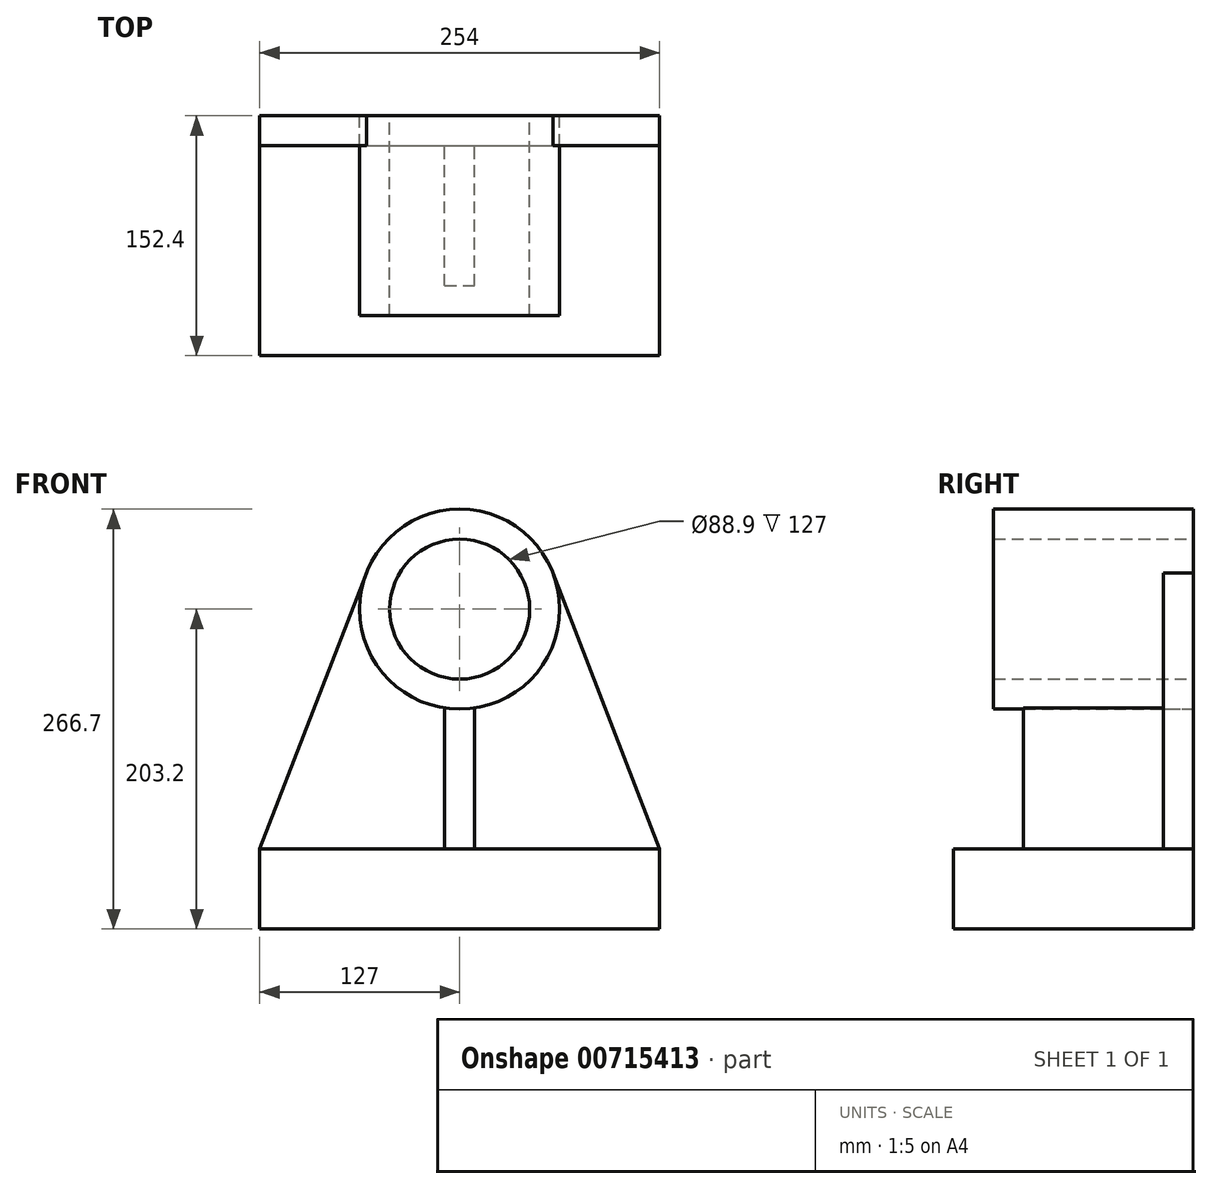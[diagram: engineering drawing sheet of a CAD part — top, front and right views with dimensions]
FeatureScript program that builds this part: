
annotation { "Feature Type Name" : "Feature", "Feature Type Description" : "" }
export const myFeature = defineFeature(function(context is Context, id is Id, definition is map)
    precondition{}
    {
        {
            var Q0;
            Q0=qCreatedBy(makeId("Front.planeOp"),FACE);
            var sketch = newSketch(context, id + "F0", { "sketchPlane" : qUnion([Q0])});
            skCircle(sketch, "E0", {"center": v(0, 0) * mm, "radius": 63.5 * mm});
            skCircle(sketch, "E1", {"center": v(0, 0) * mm, "radius": 44.45 * mm});
            skSolve(sketch);
        }
        {
            var Q0;
            Q0=makeQuery(id+"F0.imprint","IMPRINT",FACE,{"disambiguationData":[TD([[makeQuery(id+"F0.imprint","IMPRINT",EDGE,{"derivedFrom":sQuery(id+"F0.wireOp",EDGE,"E0")}),1.0]])]});
            extrude(context, id + "F1", {"entities" : qUnion([Q0]), "depth" : 127 * mm, "offsetDistance" : 25.4 * mm});
        }
        {
            var Q0;
            Q0=qCreatedBy(makeId("Front.planeOp"),FACE);
            var sketch = newSketch(context, id + "F2", { "sketchPlane" : qUnion([Q0])});
            skLineSegment(sketch, "E2", {"start": v(-59.23, 22.9) * mm, "end": v(-127, -152.4) * mm});
            skLineSegment(sketch, "E3", {"start": v(-127, -152.4) * mm, "end": v(127, -152.4) * mm});
            skLineSegment(sketch, "E4", {"start": v(127, -152.4) * mm, "end": v(59.23, 22.9) * mm});
            skArc(sketch, "E5", {"start": v(-59.23, 22.9) * mm, "mid": v(0, -63.5) * mm, "end": v(59.23, 22.9) * mm});
            skSolve(sketch);
        }
        {
            var Q0;
            Q0 = qSketchRegion(id + "F2", true);
            extrude(context, id + "F3", {"entities" : qUnion([Q0]), "depth" : 19.05 * mm, "offsetDistance" : 25.4 * mm});
        }
        {
            var Q0;
            Q0=qCreatedBy(makeId("Front.planeOp"),FACE);
            var sketch = newSketch(context, id + "F4", { "sketchPlane" : qUnion([Q0])});
            skLineSegment(sketch, "E6.bottom", {"start": v(-127, -152.4) * mm, "end": v(127, -152.4) * mm});
            skLineSegment(sketch, "E6.top", {"start": v(-127, -203.2) * mm, "end": v(127, -203.2) * mm});
            skLineSegment(sketch, "E6.left", {"start": v(-127, -152.4) * mm, "end": v(-127, -203.2) * mm});
            skLineSegment(sketch, "E6.right", {"start": v(127, -152.4) * mm, "end": v(127, -203.2) * mm});
            skSolve(sketch);
        }
        {
            var Q0;
            Q0=makeQuery(id+"F4.imprint","IMPRINT",FACE,{"disambiguationData":[TD([[makeQuery(id+"F4.imprint","IMPRINT",EDGE,{"derivedFrom":sQuery(id+"F4.wireOp",EDGE,"E6.bottom")}),-1.0]])]});
            extrude(context, id + "F5", {"entities" : qUnion([Q0]), "operationType" : NewBodyOperationType.ADD, "depth" : 152.4 * mm, "offsetDistance" : 25.4 * mm});
        }
        {
            var Q0;
            Q0=makeQuery(id+"F3.opExtrude","CAP_FACE",FACE,{"disambiguationData":[OSD([sQuery(id+"F2.wireOp",EDGE,"E2"),sQuery(id+"F2.wireOp",EDGE,"E3"),sQuery(id+"F2.wireOp",EDGE,"E4"),sQuery(id+"F2.wireOp",EDGE,"E5")])],"isStart":false});
            var sketch = newSketch(context, id + "F6", { "sketchPlane" : qUnion([Q0])});
            skLineSegment(sketch, "E7", {"start": v(-9.53, -152.4) * mm, "end": v(9.53, -152.4) * mm});
            skLineSegment(sketch, "E8", {"start": v(9.53, -152.4) * mm, "end": v(9.53, -62.78) * mm});
            skLineSegment(sketch, "E9", {"start": v(-9.53, -152.4) * mm, "end": v(-9.53, -62.78) * mm});
            skArc(sketch, "E10", {"start": v(-9.53, -62.78) * mm, "mid": v(0, -63.5) * mm, "end": v(9.53, -62.78) * mm});
            skSolve(sketch);
        }
        {
            var Q0;
            Q0=makeQuery(id+"F6.imprint","IMPRINT",FACE,{"disambiguationData":[TD([[makeQuery(id+"F6.imprint","IMPRINT",EDGE,{"derivedFrom":sQuery(id+"F6.wireOp",EDGE,"E7")}),1.0]])]});
            extrude(context, id + "F7", {"entities" : qUnion([Q0]), "depth" : 88.9 * mm, "offsetDistance" : 25.4 * mm});
        }
    });
